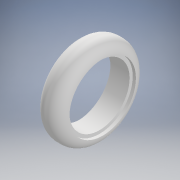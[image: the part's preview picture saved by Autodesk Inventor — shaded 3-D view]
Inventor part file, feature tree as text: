
AUTODESK INVENTOR PART (.ipt)
format: ipt  version: 2020 (Build 240168000, 168)  size: 311,808 bytes
history: native  units: mm
features: chamfer x10, sketch x6, extrude x6, fillet x1, other x1, pattern_circular x1
ambient origin geometry x8: Origin, YZ Plane, XZ Plane, XY Plane, X Axis, Y Axis, Z Axis, Center Point
bodies: Solid1 (feature_tree)
feature tree (25):
  sketch  "Sketch1"  dims[d0=27.5mm d1=19.0mm]
  sketch  "Sketch2"  dims[d2=5.0mm d3=21.0mm d4=6.0mm d5=0.0mm]
  extrude  "Extrusion1"  Depth=19.0mm
  extrude  "Extrusion2"  Depth=21.0mm
  fillet  "Fillet1"  Radius=6.0mm
  extrude  "Extrusion5"  Depth=4.0mm
  extrude  "Extrusion7"  Depth=1.0mm TaperAngle=0.0deg
  extrude  "Extrusion8"  Depth=2.0mm TaperAngle=0.0deg
  extrude  "Extrusion9"  Depth=0.5mm TaperAngle=0.0deg
  other  "Work Axis10"
  pattern_circular  "Circular Pattern2"  [2 undecoded]
  chamfer  "Chamfer2"  Distance=100.0mm Angle=360.0deg
  chamfer  "Chamfer3"  Distance=0.22mm Angle=45.0deg
  chamfer  "Chamfer4"  Distance=0.22mm Angle=45.0deg
  chamfer  "Chamfer5"  Distance=0.22mm Angle=45.0deg
  chamfer  "Chamfer6"  Distance=0.22mm Angle=45.0deg
  chamfer  "Chamfer7"  Distance=0.22mm Angle=45.0deg
  chamfer  "Chamfer8"  Distance=0.22mm Angle=45.0deg
  chamfer  "Chamfer9"  Distance=0.22mm Angle=45.0deg
  chamfer  "Chamfer10"  Distance=0.22mm Angle=45.0deg
  chamfer  "Chamfer11"  Distance=0.22mm Angle=45.0deg
  sketch  "Sketch9"  dims[d6=8.0mm d7=0.0mm d8=4.0mm]
  sketch  "Sketch11"  dims[d24=17.0mm d25=1.0mm d26=0.0mm]
  sketch  "Sketch12"  dims[d30=20.0mm d31=2.0mm d32=0.0mm]
  sketch  "Sketch14"  dims[d33=18.5mm d34=0.5mm d35=0.0mm d39=2.0mm d40=0.0mm d41=100.0mm d42=360.0deg d44=0.22mm d45=0.4mm d46=45.0deg d47=0.22mm d48=0.4mm d49=45.0deg d50=0.22mm d51=0.4mm d52=45.0deg d53=0.22mm d54=0.4mm d55=45.0deg d56=0.22mm d57=0.4mm d58=45.0deg d59=0.22mm d60=0.4mm d61=45.0deg d62=0.22mm d63=0.4mm d64=45.0deg d65=0.22mm d66=0.4mm d67=45.0deg d68=0.22mm d69=0.4mm d70=45.0deg d71=0.22mm d72=0.4mm d73=45.0deg d27=0.872665mm]
note: 2 required parameter values undecoded (feature->parameter linkage not recoverable at this tier; creation-order binding heuristic only, values carry confidence <= 0.55)
